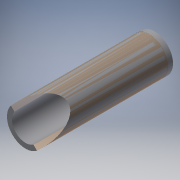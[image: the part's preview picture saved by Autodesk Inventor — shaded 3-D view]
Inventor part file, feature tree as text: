
AUTODESK INVENTOR PART (.ipt)
format: ipt  version: 2016 (Build 200138000, 138)  size: 115,712 bytes
history: native  units: in
note: dims shown in document units (in); Inventor stores cm internally (conversion verified against a paired STEP export)
features: thicken_offset x2, sketch x1, other x1, extrude x1
ambient origin geometry x8: Origin, YZ Plane, XZ Plane, XY Plane, X Axis, Y Axis, Z Axis, Center Point
bodies: Solid1 (feature_tree), Solid2 (feature_tree)
feature tree (5):
  thicken_offset  "Thicken1"
  thicken_offset  "Thicken2"
  sketch  "Sketch1"  dims[d0=0.075in d1=0.25in d2=0.0in d3=0.01in d4=0.01in d5=0.01in d6=0.01in]
  other  "Srf1"
  extrude  "ExtrusionSrf1"  Depth=0.25in TaperAngle=0.0deg
